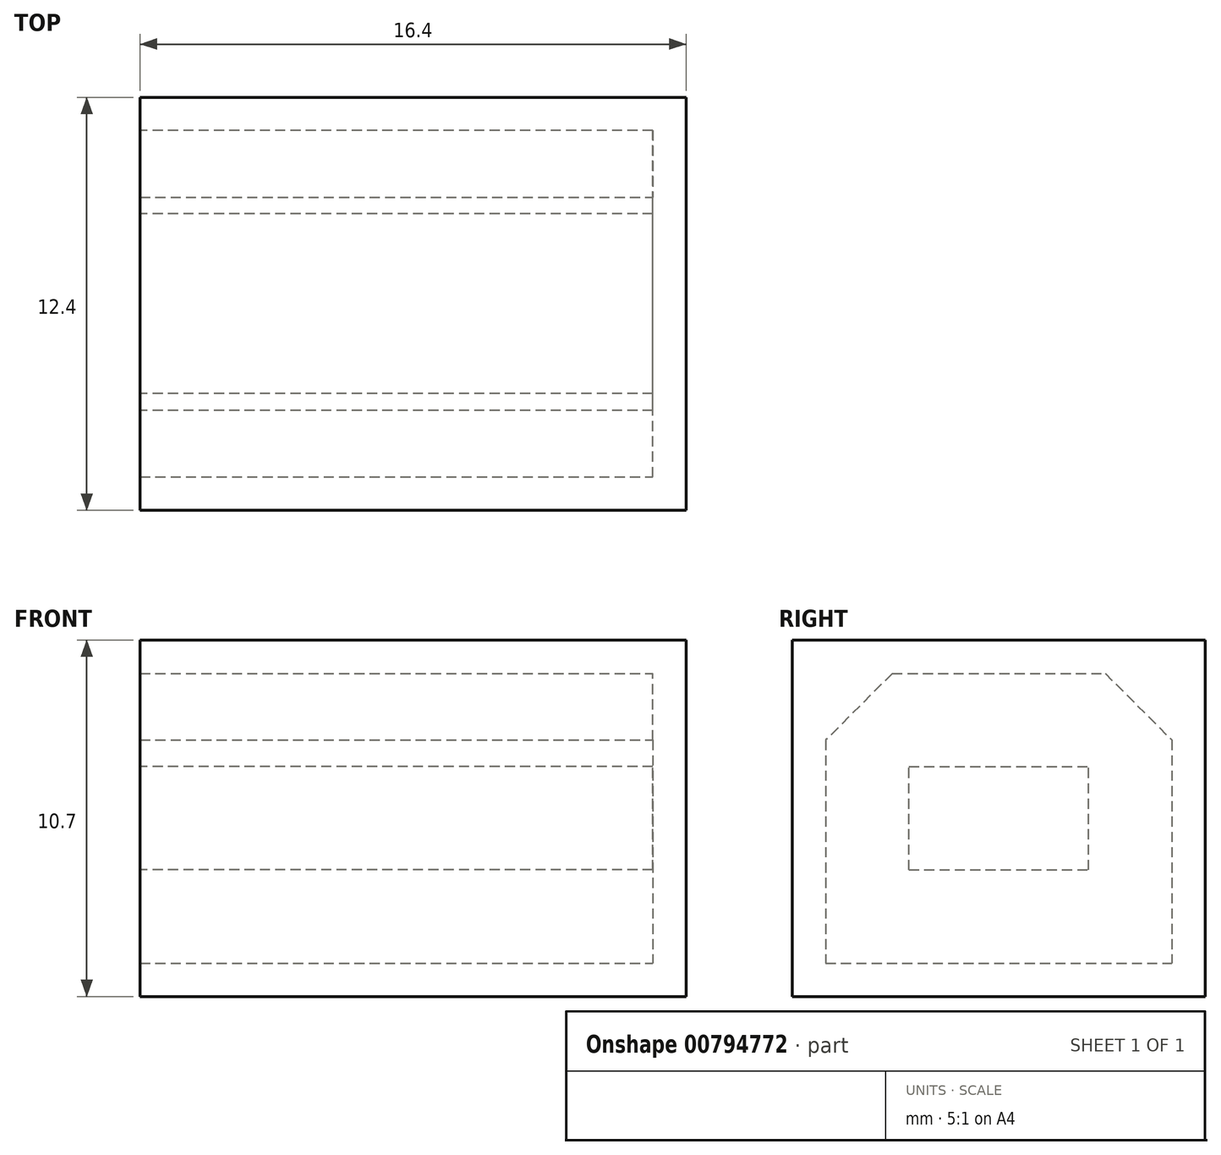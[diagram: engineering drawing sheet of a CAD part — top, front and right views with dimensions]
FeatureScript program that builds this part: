
annotation { "Feature Type Name" : "Feature", "Feature Type Description" : "" }
export const myFeature = defineFeature(function(context is Context, id is Id, definition is map)
    precondition{}
    {
        {
            var Q0;
            Q0=qCreatedBy(makeId("Top.planeOp"),FACE);
            var sketch = newSketch(context, id + "F0", { "sketchPlane" : qUnion([Q0])});
            skLineSegment(sketch, "E0.bottom", {"start": v(0, 0) * mm, "end": v(16.4, 0) * mm});
            skLineSegment(sketch, "E0.top", {"start": v(0, 12.4) * mm, "end": v(16.4, 12.4) * mm});
            skLineSegment(sketch, "E0.left", {"start": v(0, 0) * mm, "end": v(0, 12.4) * mm});
            skLineSegment(sketch, "E0.right", {"start": v(16.4, 0) * mm, "end": v(16.4, 12.4) * mm});
            skLineSegment(sketch, "E1", {"start": v(-2.29, 6.2) * mm, "end": v(19.72, 6.2) * mm, "construction": true});
            skPoint(sketch, "E2", {"position": v(16.4, 6.2) * mm});
            skSolve(sketch);
        }
        {
            var Q0;
            Q0=makeQuery(id+"F0.imprint","IMPRINT",FACE,{"disambiguationData":[TD([[makeQuery(id+"F0.imprint","IMPRINT",EDGE,{"derivedFrom":sQuery(id+"F0.wireOp",EDGE,"E0.bottom")}),1.0]])]});
            extrude(context, id + "F1", {"entities" : qUnion([Q0]), "depth" : 10.7 * mm, "offsetDistance" : 25 * mm});
        }
        {
            var Q0;
            Q0=makeQuery(id+"F1.opExtrude","SWEPT_FACE",FACE,{"disambiguationData":[OSD([sQuery(id+"F0.wireOp",EDGE,"E0.left")])]});
            shell(context, id + "F2", {"entities" : qUnion([Q0]), "thickness" : 1 * mm});
        }
        {
            var Q0;
            Q0=makeQuery(id+"F1.opExtrude","SWEPT_FACE",FACE,{"disambiguationData":[OSD([sQuery(id+"F0.wireOp",EDGE,"E0.left")])]});
            var sketch = newSketch(context, id + "F3", { "sketchPlane" : qUnion([Q0])});
            skLineSegment(sketch, "E3.bottom", {"start": v(-8.9, 6.9) * mm, "end": v(-3.5, 6.9) * mm});
            skLineSegment(sketch, "E3.top", {"start": v(-8.9, 3.8) * mm, "end": v(-3.5, 3.8) * mm});
            skLineSegment(sketch, "E3.left", {"start": v(-8.9, 6.9) * mm, "end": v(-8.9, 3.8) * mm});
            skLineSegment(sketch, "E3.right", {"start": v(-3.5, 6.9) * mm, "end": v(-3.5, 3.8) * mm});
            skLineSegment(sketch, "E4", {"start": v(-6.2, -2.04) * mm, "end": v(-6.2, 12.97) * mm, "construction": true});
            skPoint(sketch, "E4.startSnap0", {"position": v(-6.2, 0) * mm});
            skLineSegment(sketch, "E5", {"start": v(-15.35, 5.35) * mm, "end": v(4.53, 5.35) * mm, "construction": true});
            skPoint(sketch, "E5.startSnap0", {"position": v(-12.4, 5.35) * mm});
            skSolve(sketch);
        }
        {
            var Q0;
            Q0=makeQuery(id+"F3.imprint","IMPRINT",FACE,{"disambiguationData":[TD([[makeQuery(id+"F3.imprint","IMPRINT",EDGE,{"derivedFrom":sQuery(id+"F3.wireOp",EDGE,"E3.bottom")}),-1.0]])]});
            extrude(context, id + "F4", {"entities" : qUnion([Q0]), "operationType" : NewBodyOperationType.ADD, "endBound" : BoundingType.UP_TO_NEXT, "oppositeDirection" : true, "depth" : 25 * mm, "offsetDistance" : 25 * mm});
        }
        {
            var Q0;
            {var subQ0=sQuery(id+"F0.wireOp",EDGE,"E0.top");Q0=makeQuery(id+"F2.opShell","OFFSET_EDGE",EDGE,{"disambiguationData":[OSD([subQ0]),TDD([makeQuery(id+"F1.opExtrude","CAP_EDGE",EDGE,{"disambiguationData":[OSD([subQ0])],"isStart":false})])]});}
            var Q1;
            {var subQ0=sQuery(id+"F0.wireOp",EDGE,"E0.bottom");Q1=makeQuery(id+"F2.opShell","OFFSET_EDGE",EDGE,{"disambiguationData":[OSD([subQ0]),TDD([makeQuery(id+"F1.opExtrude","CAP_EDGE",EDGE,{"disambiguationData":[OSD([subQ0])],"isStart":false})])]});}
            chamfer(context, id + "F5", {"entities" : qUnion([Q0, Q1]), "width" : 2 * mm, "tangentPropagation" : true});
        }
    });
